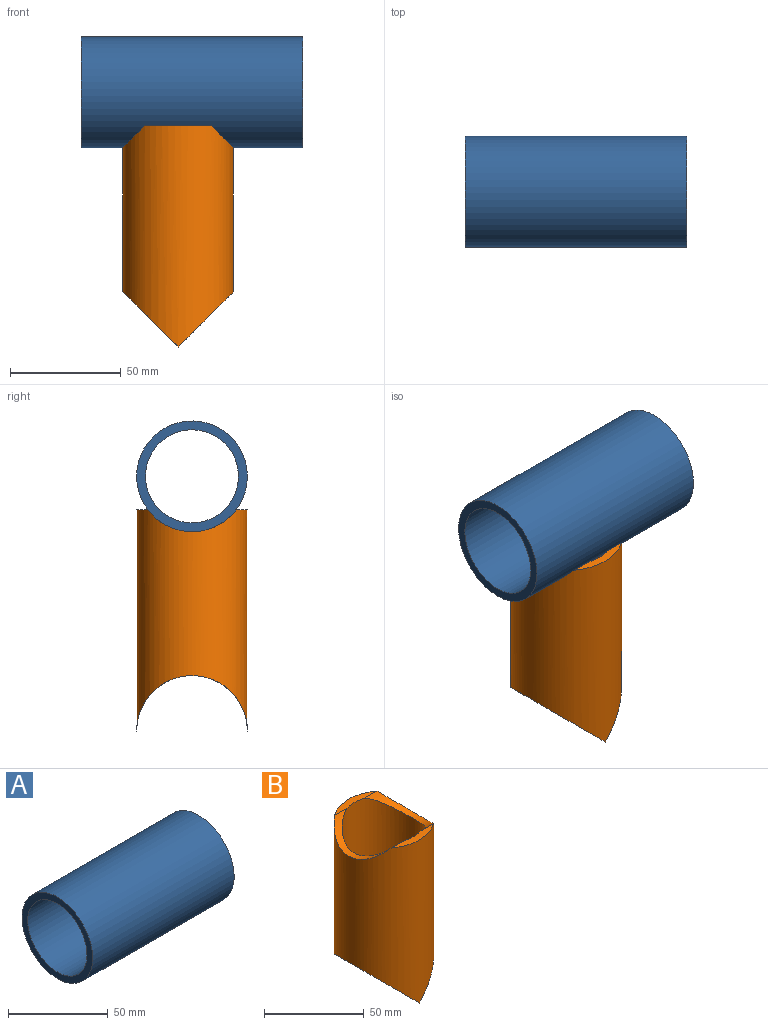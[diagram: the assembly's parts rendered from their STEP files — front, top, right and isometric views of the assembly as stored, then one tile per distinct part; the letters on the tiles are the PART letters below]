
ASSEMBLY  parts=2 mates=1
PART A: 4 faces, bbox 100x50x50 mm
  f0: cylinder r=21mm len=100mm, axis (-1,0,0), area 13194.7mm2, adj f2,f3
  f1: cylinder r=25mm len=100mm, axis (-1,0,0), area 15708mm2, adj f2,f3
  f2: plane 50x50mm, normal (1,0,0), area 578.1mm2, adj f0,f1
  f3: plane 50x50mm, normal (-1,0,0), area 578.1mm2, adj f0,f1
PART B: 7 faces, bbox 50.1x50x100 mm
  f0: plane 30x5mm, normal (0,0,1), area 93.6mm2, adj f1,f2,f4,f5
  f1: cylinder r=21mm len=86.44mm, axis (0,0,-1), area 9948.4mm2, adj f0,f3,f4,f5,f6
  f2: cylinder r=25mm len=100mm, axis (0,0,-1), area 12598.9mm2, adj f0,f3,f4,f5,f6
  f3: plane 30x5mm, normal (0,0,1), area 93.6mm2, adj f1,f2,f4,f5
  f4: cylinder r=25mm len=40mm, axis (1,0,0), area 233.8mm2, adj f0,f1,f2,f3
  f5: cylinder r=25mm len=40mm, axis (1,0,0), area 233.7mm2, adj f0,f1,f2,f3
  f6: cylinder r=25mm len=50.13mm, axis (1,0,0), area 937.7mm2, adj f1,f2
PLACE A at identity
PLACE B t=(43.71,100,-115)mm
MATE fastened B.f4 <-> A.f0  axis (1,0,0) through (50,100,0)mm
